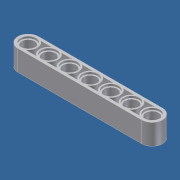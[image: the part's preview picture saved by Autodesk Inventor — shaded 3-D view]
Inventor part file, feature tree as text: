
AUTODESK INVENTOR PART (.ipt)
format: ipt  version: 2016 SP1 (Build 200210100, 210)  size: 207,360 bytes
history: native  units: mm
features: extrude x5, sketch x5
ambient origin geometry x8: Origin, YZ Plane, XZ Plane, XY Plane, X Axis, Y Axis, Z Axis, Center Point
bodies: Solid1 (feature_tree)
feature tree (10):
  extrude  "Extrusion1"  Depth=4.0mm
  extrude  "Extrusion10"  TaperAngle=0.0deg  [1 undecoded]
  extrude  "Extrusion11"  TaperAngle=180.0deg  [1 undecoded]
  extrude  "Extrusion12"  Depth=8.0mm TaperAngle=0.0deg
  extrude  "Extrusion13"  Depth=0.8mm
  sketch  "Sketch2"  dims[d0=4.0mm d1=4.0mm]
  sketch  "Sketch11"  dims[d2=48.0mm d3=0.0mm]
  sketch  "Sketch12"  dims[d4=24.0mm d9=180.0deg]
  sketch  "Sketch13"  dims[d10=0.0mm d12=8.0mm d13=0.0mm]
  sketch  "Sketch14"  dims[d98=48.0mm d99=5.0mm d100=10.0mm d102=10.0mm d103=70.0mm d105=8.0mm d107=0.8mm d108=0.0mm d109=6.0mm d110=10.0mm d112=10.0mm d113=70.0mm d115=8.0mm d117=0.8mm d118=0.0mm d119=6.0mm d120=10.0mm d122=10.0mm d123=70.0mm d125=8.0mm d127=0.8mm d128=0.0mm d129=7.0mm d131=7.0mm d132=10.0mm d134=10.0mm d135=60.0mm d137=8.0mm d139=0.8mm d140=0.0mm]
note: 2 required parameter values undecoded (feature->parameter linkage not recoverable at this tier; creation-order binding heuristic only, values carry confidence <= 0.55)
